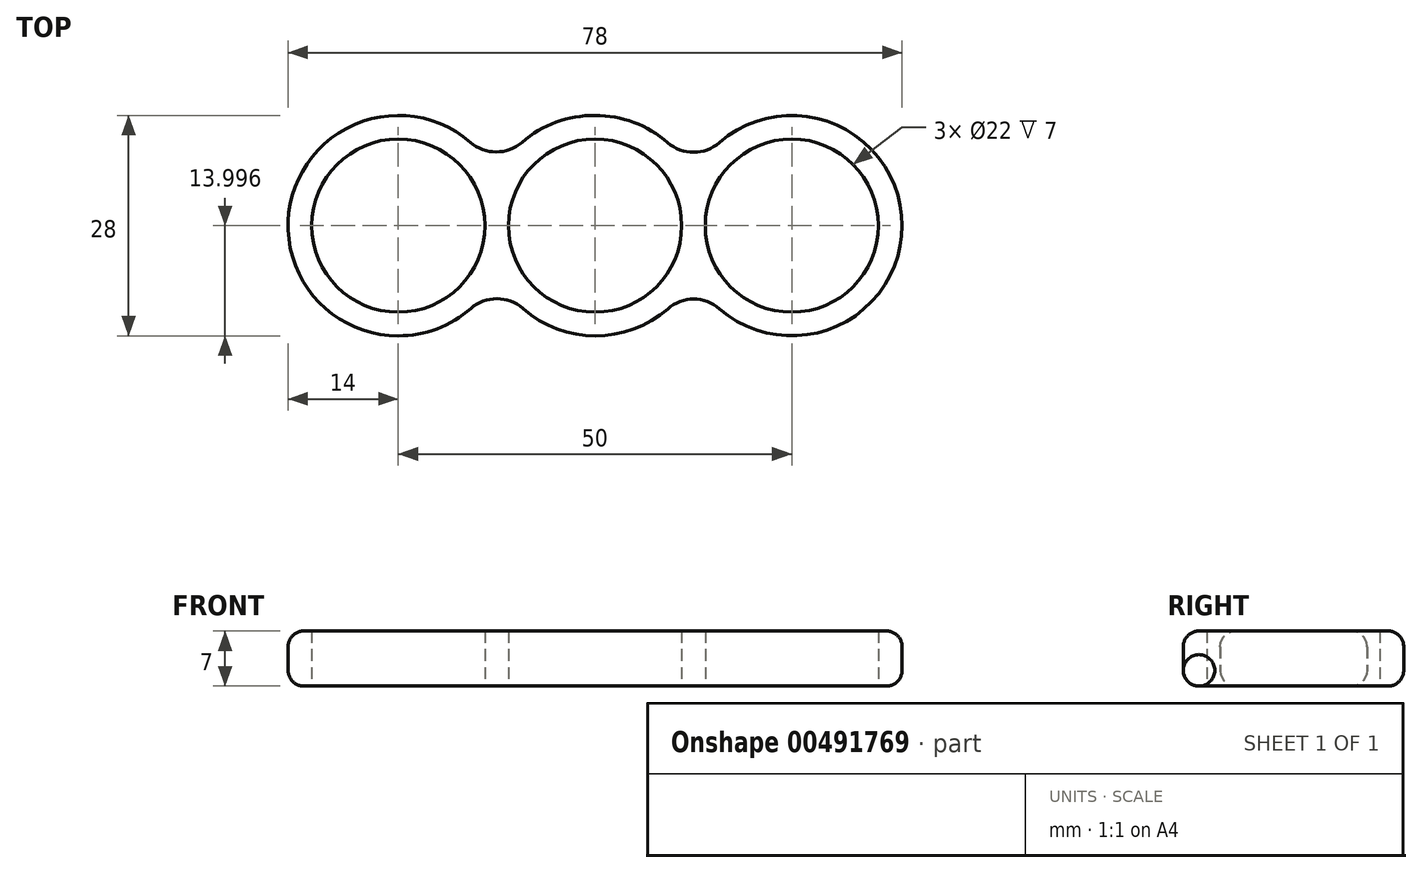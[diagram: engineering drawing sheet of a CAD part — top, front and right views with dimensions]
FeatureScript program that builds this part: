
annotation { "Feature Type Name" : "Feature", "Feature Type Description" : "" }
export const myFeature = defineFeature(function(context is Context, id is Id, definition is map)
    precondition{}
    {
        {
            var Q0;
            Q0=qCreatedBy(makeId("Top.planeOp"),FACE);
            var sketch = newSketch(context, id + "F0", { "sketchPlane" : qUnion([Q0])});
            skLineSegment(sketch, "E0.bottom", {"start": v(-0.25, 13.77) * mm, "end": v(0.05, 13.77) * mm});
            skLineSegment(sketch, "E0.top", {"start": v(0, -14.23) * mm, "end": v(0.1, -14.23) * mm});
            skArc(sketch, "E1", {"start": v(-25, 13.77) * mm, "mid": v(-39, -0.23) * mm, "end": v(-25, -14.23) * mm});
            skArc(sketch, "E2", {"start": v(25, -14.23) * mm, "mid": v(39, -0.23) * mm, "end": v(25, 13.77) * mm});
            skCircle(sketch, "E3", {"center": v(-25, -0.23) * mm, "radius": 11 * mm});
            skCircle(sketch, "E4", {"center": v(25, -0.23) * mm, "radius": 11 * mm});
            skCircle(sketch, "E5", {"center": v(0, -0.23) * mm, "radius": 11 * mm});
            skArc(sketch, "E6", {"start": v(-15.84, 10.35) * mm, "mid": v(-20.1, 12.88) * mm, "end": v(-25, 13.77) * mm});
            skArc(sketch, "E7", {"start": v(25, 13.77) * mm, "mid": v(20.09, 12.88) * mm, "end": v(15.8, 10.32) * mm});
            skLineSegment(sketch, "E8", {"start": v(0, 24.33) * mm, "end": v(0, -25.05) * mm, "construction": true});
            skArc(sketch, "E9", {"start": v(0, 13.77) * mm, "mid": v(-4.96, 12.9) * mm, "end": v(-9.29, 10.35) * mm});
            skArc(sketch, "E10", {"start": v(9.23, 10.32) * mm, "mid": v(4.93, 12.88) * mm, "end": v(0, 13.77) * mm});
            skPoint(sketch, "E11.newPointB", {"position": v(0, -14.23) * mm});
            skArc(sketch, "E11.filletArc", {"start": v(-15.84, 10.35) * mm, "mid": v(-12.56, 9.13) * mm, "end": v(-9.29, 10.35) * mm});
            skArc(sketch, "E12.filletArc", {"start": v(9.23, 10.32) * mm, "mid": v(12.51, 9.09) * mm, "end": v(15.8, 10.32) * mm});
            skArc(sketch, "E13", {"start": v(-25, -14.23) * mm, "mid": v(-20.07, -13.34) * mm, "end": v(-15.77, -10.76) * mm});
            skArc(sketch, "E14", {"start": v(15.8, -10.8) * mm, "mid": v(20.1, -13.35) * mm, "end": v(25, -14.23) * mm});
            skArc(sketch, "E15", {"start": v(0, -14.23) * mm, "mid": v(4.93, -13.35) * mm, "end": v(9.24, -10.8) * mm});
            skArc(sketch, "E16", {"start": v(-9.18, -10.76) * mm, "mid": v(-4.9, -13.33) * mm, "end": v(0, -14.23) * mm});
            skArc(sketch, "E17.filletArc", {"start": v(-9.18, -10.76) * mm, "mid": v(-12.47, -9.52) * mm, "end": v(-15.77, -10.76) * mm});
            skArc(sketch, "E18.filletArc", {"start": v(15.8, -10.8) * mm, "mid": v(12.53, -9.57) * mm, "end": v(9.24, -10.8) * mm});
            skSolve(sketch);
        }
        {
            var Q0;
            Q0 = qSketchRegion(id + "F0", true);
            extrude(context, id + "F1", {"entities" : qUnion([Q0]), "depth" : 7 * mm});
        }
        {
            var Q0;
            Q0=makeQuery(id+"F1.opExtrude","SWEPT_FACE",FACE,{"disambiguationData":[OSD([sQuery(id+"F0.wireOp",EDGE,"E1"),sQuery(id+"F0.wireOp",EDGE,"E6")])]});
            var Q1;
            Q1=makeQuery(id+"F1.opExtrude","SWEPT_FACE",FACE,{"disambiguationData":[OSD([sQuery(id+"F0.wireOp",EDGE,"E13")])]});
            var Q2;
            Q2=makeQuery(id+"F1.opExtrude","SWEPT_FACE",FACE,{"disambiguationData":[OSD([sQuery(id+"F0.wireOp",EDGE,"E17.filletArc")])]});
            var Q3;
            Q3=makeQuery(id+"F1.opExtrude","SWEPT_FACE",FACE,{"disambiguationData":[OSD([sQuery(id+"F0.wireOp",EDGE,"E15"),sQuery(id+"F0.wireOp",EDGE,"E16")])]});
            var Q4;
            Q4=makeQuery(id+"F1.opExtrude","SWEPT_FACE",FACE,{"disambiguationData":[OSD([sQuery(id+"F0.wireOp",EDGE,"E18.filletArc")])]});
            var Q5;
            Q5=makeQuery(id+"F1.opExtrude","SWEPT_FACE",FACE,{"disambiguationData":[OSD([sQuery(id+"F0.wireOp",EDGE,"E2"),sQuery(id+"F0.wireOp",EDGE,"E7"),sQuery(id+"F0.wireOp",EDGE,"E14")])]});
            var Q6;
            Q6=makeQuery(id+"F1.opExtrude","SWEPT_FACE",FACE,{"disambiguationData":[OSD([sQuery(id+"F0.wireOp",EDGE,"E11.filletArc")])]});
            var Q7;
            Q7=makeQuery(id+"F1.opExtrude","SWEPT_FACE",FACE,{"disambiguationData":[OSD([sQuery(id+"F0.wireOp",EDGE,"E9")])]});
            var Q8;
            Q8=makeQuery(id+"F1.opExtrude","SWEPT_FACE",FACE,{"disambiguationData":[OSD([sQuery(id+"F0.wireOp",EDGE,"E10")])]});
            var Q9;
            Q9=makeQuery(id+"F1.opExtrude","SWEPT_FACE",FACE,{"disambiguationData":[OSD([sQuery(id+"F0.wireOp",EDGE,"E12.filletArc")])]});
            fillet(context, id + "F2", {"entities" : qUnion([Q0, Q1, Q2, Q3, Q4, Q5, Q6, Q7, Q8, Q9]), "radius" : 2 * mm, "tangentPropagation" : true, "allowEdgeOverflow" : false});
        }
    });
